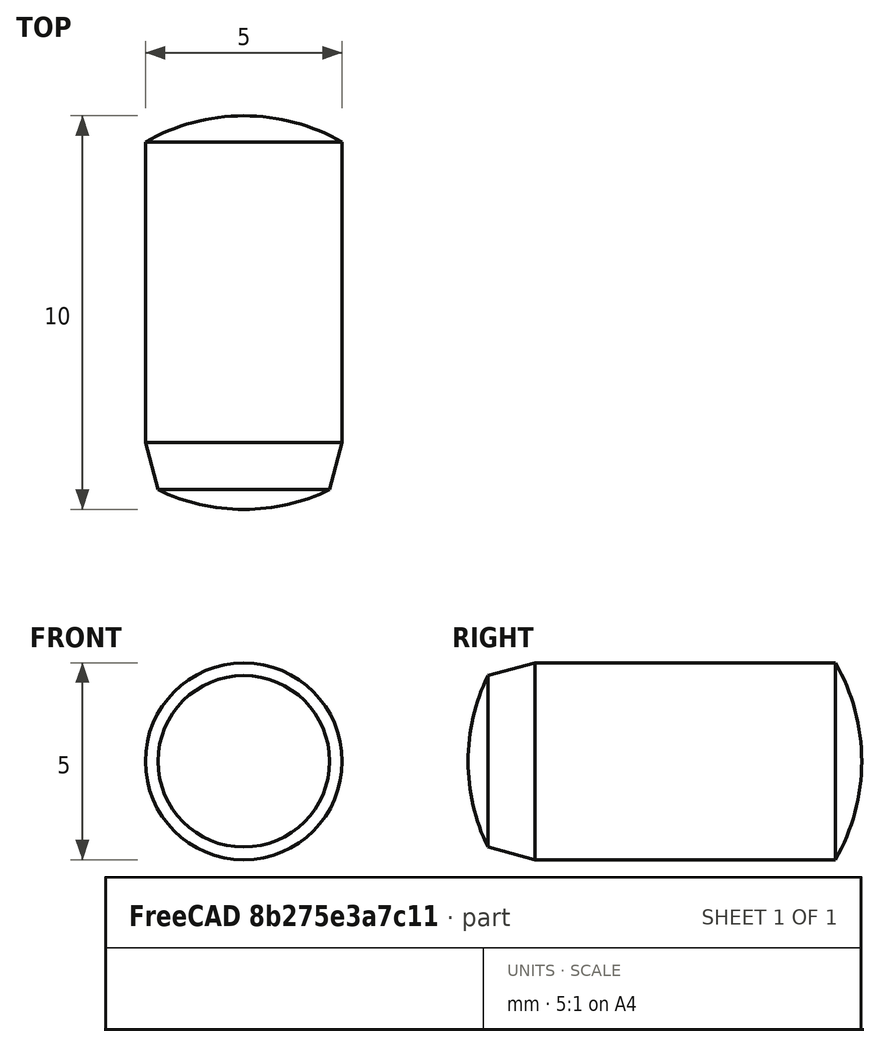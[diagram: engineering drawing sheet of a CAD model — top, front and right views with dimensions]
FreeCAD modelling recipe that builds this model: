
FCSTD DOCUMENT  (FreeCAD 0.15R4470 (Git))
Label: Zyl-Stift_DIN_6325-5x10
License: CC-BY 3.0
LicenseURL: http://creativecommons.org/licenses/by/3.0/
objects: Sketcher::SketchObject×1, PartDesign::Revolution×1
note: 3 computed .brp shape members not serialized (recipe doc carries the construction recipe); baked Part::Feature solids carry a one-line shape summary decoded from their .brp

FEATURE [Sketcher::SketchObject] Sketch
  Placement = pos=(0,0,0) rot=(0.57735,0.57735,0.57735;2.0944rad)
  sketch-geometry (5):
    g0: ArcOfCircle CenterX=4.49569 CenterY=0 CenterZ=0 NormalX=0 NormalY=0 NormalZ=1 Radius=4.99569 StartAngle=2.69037 EndAngle=3.14159
    g1: LineSegment StartX=0 StartY=2.17846 StartZ=0 EndX=1.2 EndY=2.5 EndZ=0
    g2: LineSegment StartX=1.2 StartY=2.5 StartZ=0 EndX=8.82946 EndY=2.5 EndZ=0
    g3: ArcOfCircle CenterX=4.50431 CenterY=0 CenterZ=0 NormalX=0 NormalY=0 NormalZ=1 Radius=4.99569 StartAngle=0 EndAngle=0.524097
    g4: LineSegment StartX=-0.5 StartY=0 StartZ=0 EndX=9.5 EndY=0 EndZ=0
  constraints (17):
    c: PointOnObject(g0,g-1)
    c: PointOnObject(g0,g-1)
    c: PointOnObject(g0,g-2)
    c: Coincident(g0,g1)
    c: Coincident(g1,g2)
    c: Horizontal(g2)
    c: PointOnObject(g3,g-1)
    c: Coincident(g3,g2)
    c: PointOnObject(g3,g-1)
    c: Coincident(g4,g0)
    c: Coincident(g4,g3)
    c: Equal(g0,g3)
    c: Angle(g4,g1) = 0.261799
    c: DistanceX(g4) = 10
    c: DistanceY(g-1,g1) = 2.5
    c: DistanceX(g1) = 1.2
    c: DistanceX(g0,g0) = 0.5
FEATURE [PartDesign::Revolution] Revolution  label="Zyl-Stift DIN 6325-5x10 #"
  Angle = 360
  Axis = (0,1,0)
  Base = (0,0,0)
  Placement = pos=(0,0,0) rot=(0.57735,0.57735,0.57735;2.0944rad)
  ReferenceAxis = -> Sketch [H_Axis]
  Sketch = -> Sketch
